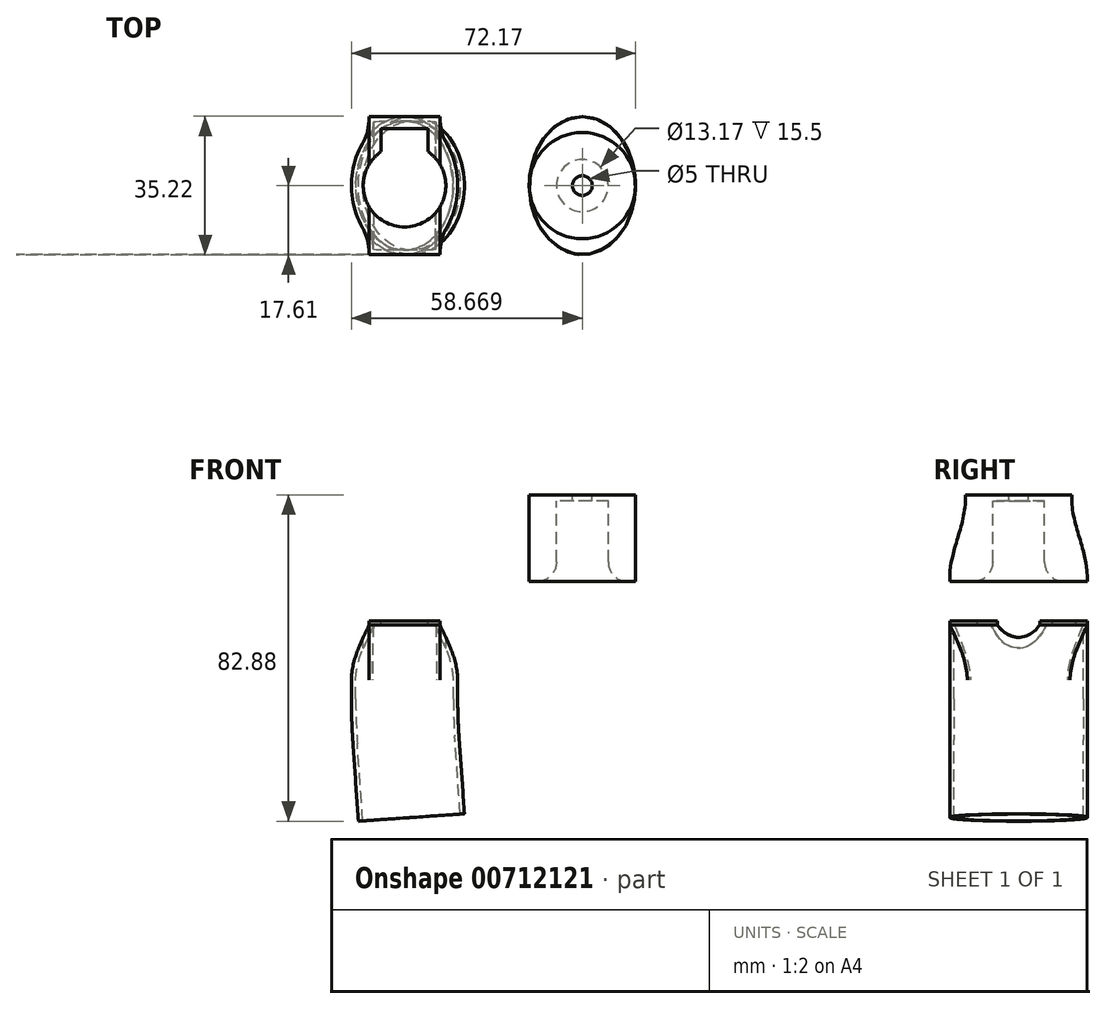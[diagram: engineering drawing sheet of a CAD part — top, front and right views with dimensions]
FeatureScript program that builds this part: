
annotation { "Feature Type Name" : "Feature", "Feature Type Description" : "" }
export const myFeature = defineFeature(function(context is Context, id is Id, definition is map)
    precondition{}
    {
        {
            var Q0;
            Q0=qCreatedBy(makeId("Top.planeOp"),FACE);
            var sketch = newSketch(context, id + "F0", { "sketchPlane" : qUnion([Q0])});
            skLineSegment(sketch, "E0.bottom", {"start": v(-9, 17.5) * mm, "end": v(9, 17.5) * mm});
            skLineSegment(sketch, "E0.top", {"start": v(-9, -17.5) * mm, "end": v(9, -17.5) * mm});
            skLineSegment(sketch, "E0.left", {"start": v(-9, 17.5) * mm, "end": v(-9, -17.5) * mm});
            skLineSegment(sketch, "E0.right", {"start": v(9, 17.5) * mm, "end": v(9, -17.5) * mm});
            skSolve(sketch);
        }
        {
            var Q0;
            Q0=makeQuery(id+"F0.imprint","IMPRINT",FACE,{"disambiguationData":[TD([[makeQuery(id+"F0.imprint","IMPRINT",EDGE,{"derivedFrom":sQuery(id+"F0.wireOp",EDGE,"E0.bottom")}),-1.0]])]});
            extrude(context, id + "F1", {"entities" : qUnion([Q0]), "depth" : 15 * mm, "offsetDistance" : 25 * mm, "hasSecondDirection" : true, "secondDirectionOppositeDirection" : false, "secondDirectionDepth" : 14 * mm});
        }
        {
            var Q0;
            Q0=qCreatedBy(makeId("Top.planeOp"),FACE);
            var sketch = newSketch(context, id + "F2", { "sketchPlane" : qUnion([Q0])});
            skEllipticalArc(sketch, "E1", {});
            skEllipticalArc(sketch, "E2", {});
            skEllipticalArc(sketch, "E3", {});
            skEllipticalArc(sketch, "E4", {});
            const initialGuessF2  = {"E1": [0, 0, 0, 1, 0.0175, 0.0135, 3.8715789062969574, 5.5567192780219345], "E2": [0, 0, 0, 1, 0.0175, 0.0135, 2.4065715334507507, 3.8715789062969574], "E3": [0, 0, 0, 1, 0.0175, 0.0135, 5.5567192780219345, 0.7288720705966393], "E4": [0, 0, 0, 1, 0.0175, 0.0135, 0.7288720705966393, 2.4065715334507507]};
            skSetInitialGuess(sketch, initialGuessF2);
            skSolve(sketch);
        }
        {
            var Q1;
            Q1=makeQuery(id+"F1.opExtrude","CAP_FACE",FACE,{"disambiguationData":[OSD([sQuery(id+"F0.wireOp",EDGE,"E0.bottom"),sQuery(id+"F0.wireOp",EDGE,"E0.top"),sQuery(id+"F0.wireOp",EDGE,"E0.left"),sQuery(id+"F0.wireOp",EDGE,"E0.right")])],"isStart":true});
            var Q2;
            Q2=makeQuery(id+"F2.imprint","IMPRINT",FACE,{"disambiguationData":[TD([[makeQuery(id+"F2.imprint","IMPRINT",EDGE,{"derivedFrom":sQuery(id+"F2.wireOp",EDGE,"E1")}),1.0]])]});
            loft(context, id + "F3", {"operationType" : NewBodyOperationType.ADD, "endCondition" : LoftEndDerivativeType.NORMAL_TO_PROFILE, "endMagnitude" : 1, "sheetProfilesArray" : [{ "sheetProfileEntities" : qUnion([Q1]) }, { "sheetProfileEntities" : qUnion([Q2]) }]});
        }
        {
            var Q0;
            Q0=qCreatedBy(makeId("Top.planeOp"),FACE);
            cPlane(context, id + "F4", {"entities" : qUnion([Q0]), "cplaneType" : CPlaneType.OFFSET, "offset" : 25 * mm, "width" : 150 * mm, "height" : 150 * mm});
        }
        {
            var Q0;
            Q0=makeQuery(id+"F3.opLoft","CAP_FACE",FACE,{"disambiguationData":[OSD([makeQuery(id+"F2.imprint","IMPRINT",FACE,{"disambiguationData":[TD([[makeQuery(id+"F2.imprint","IMPRINT",EDGE,{"derivedFrom":sQuery(id+"F2.wireOp",EDGE,"E1")}),1.0]])]})])],"isStart":true});
            shell(context, id + "F5", {"entities" : qUnion([Q0]), "thickness" : 1.1 * mm});
        }
        {
            var Q0;
            Q0=makeQuery(id+"F1.opExtrude","CAP_FACE",FACE,{"disambiguationData":[OSD([sQuery(id+"F0.wireOp",EDGE,"E0.bottom"),sQuery(id+"F0.wireOp",EDGE,"E0.top"),sQuery(id+"F0.wireOp",EDGE,"E0.left"),sQuery(id+"F0.wireOp",EDGE,"E0.right")])],"isStart":false});
            var sketch = newSketch(context, id + "F6", { "sketchPlane" : qUnion([Q0])});
            skCircle(sketch, "E5", {"center": v(0, 0) * mm, "radius": 10.5 * mm});
            skLineSegment(sketch, "E6.bottom", {"start": v(-6, 14.54) * mm, "end": v(6, 14.54) * mm});
            skLineSegment(sketch, "E6.top", {"start": v(-6, 7.06) * mm, "end": v(6, 7.06) * mm});
            skLineSegment(sketch, "E6.left", {"start": v(-6, 14.54) * mm, "end": v(-6, 7.06) * mm});
            skLineSegment(sketch, "E6.right", {"start": v(6, 14.54) * mm, "end": v(6, 7.06) * mm});
            skSolve(sketch);
        }
        {
            var Q0;
            {var subQ0=sQuery(id+"F6.wireOp",EDGE,"E5");var subQ1=makeQuery(id+"F1.opExtrude","CAP_EDGE",EDGE,{"disambiguationData":[OSD([sQuery(id+"F0.wireOp",EDGE,"E0.left")])],"isStart":false});var subQ2=makeQuery(id+"F6.imprint","INTERSECT",VERTEX,{"disambiguationData":[OD(0.0)],"derivedFrom":[subQ1,subQ0]});Q0=makeQuery(id+"F6.imprint","IMPRINT",FACE,{"disambiguationData":[TD([[makeQuery(id+"F6.imprint","IMPRINT",EDGE,{"disambiguationData":[TD([[subQ2,1.0]])],"derivedFrom":subQ0}),1.0]])]});}
            var Q1;
            {var subQ0=sQuery(id+"F6.wireOp",EDGE,"E5");var subQ1=makeQuery(id+"F1.opExtrude","CAP_EDGE",EDGE,{"disambiguationData":[OSD([sQuery(id+"F0.wireOp",EDGE,"E0.left")])],"isStart":false});var subQ2=makeQuery(id+"F6.imprint","INTERSECT",VERTEX,{"disambiguationData":[OD(0.0)],"derivedFrom":[subQ1,subQ0]});Q1=makeQuery(id+"F6.imprint","IMPRINT",FACE,{"disambiguationData":[TD([[makeQuery(id+"F6.imprint","IMPRINT",EDGE,{"disambiguationData":[TD([[subQ2,-1.0]])],"derivedFrom":subQ0}),1.0]])]});}
            var Q2;
            {var subQ0=sQuery(id+"F6.wireOp",EDGE,"E5");var subQ1=makeQuery(id+"F1.opExtrude","CAP_EDGE",EDGE,{"disambiguationData":[OSD([sQuery(id+"F0.wireOp",EDGE,"E0.right")])],"isStart":false});var subQ2=makeQuery(id+"F6.imprint","INTERSECT",VERTEX,{"disambiguationData":[OD(0.0)],"derivedFrom":[subQ1,subQ0]});Q2=makeQuery(id+"F6.imprint","IMPRINT",FACE,{"disambiguationData":[TD([[makeQuery(id+"F6.imprint","IMPRINT",EDGE,{"disambiguationData":[TD([[subQ2,1.0]])],"derivedFrom":subQ0}),1.0]])]});}
            var Q3;
            {var subQ5=sQuery(id+"F6.wireOp",EDGE,"E6.bottom");Q3=makeQuery(id+"F6.imprint","IMPRINT",FACE,{"disambiguationData":[TD([[makeQuery(id+"F6.imprint","IMPRINT",EDGE,{"derivedFrom":subQ5}),-1.0]])]});}
            var Q4;
            {var subQ5=sQuery(id+"F6.wireOp",EDGE,"E6.top");Q4=makeQuery(id+"F6.imprint","IMPRINT",FACE,{"disambiguationData":[TD([[makeQuery(id+"F6.imprint","IMPRINT",EDGE,{"derivedFrom":subQ5}),1.0]])]});}
            extrude(context, id + "F7", {"entities" : qUnion([Q0, Q1, Q2, Q3, Q4]), "operationType" : NewBodyOperationType.REMOVE, "oppositeDirection" : true, "depth" : 10 * mm, "offsetDistance" : 25 * mm});
        }
        {
            var Q0;
            Q0=makeQuery(id+"F3.opLoft","CAP_FACE",FACE,{"disambiguationData":[OSD([makeQuery(id+"F2.imprint","IMPRINT",FACE,{"disambiguationData":[TD([[makeQuery(id+"F2.imprint","IMPRINT",EDGE,{"derivedFrom":sQuery(id+"F2.wireOp",EDGE,"E1")}),1.0]])]})])],"isStart":true});
            var sketch = newSketch(context, id + "F8", { "sketchPlane" : qUnion([Q0])});
            skEllipse(sketch, "E7", {"center": v(0, 0) * mm, "majorRadius": 13.51 * mm, "minorRadius": 17.52 * mm, "majorAxis": v(1, 0)});
            skSolve(sketch);
        }
        {
            var Q0;
            Q0=qCreatedBy(makeId("Front.planeOp"),FACE);
            var sketch = newSketch(context, id + "F9", { "sketchPlane" : qUnion([Q0])});
            skLineSegment(sketch, "E8", {"start": v(0, 0) * mm, "end": v(0, -4.76) * mm});
            skLineSegment(sketch, "E9", {"start": v(0.37, -15.23) * mm, "end": v(1.74, -34.94) * mm});
            skPoint(sketch, "E10.visualSharp", {"position": v(0, -10) * mm});
            skArc(sketch, "E10.filletArc", {"start": v(0, -4.76) * mm, "mid": v(0.1, -10) * mm, "end": v(0.37, -15.23) * mm});
            skLineSegment(sketch, "E11", {"start": v(1.74, -34.94) * mm, "end": v(4.83, -79.09) * mm});
            skSolve(sketch);
        }
        {
            var Q0;
            {var subQ1=sQuery(id+"F2.wireOp",EDGE,"E3");var subQ2=sQuery(id+"F2.wireOp",EDGE,"E2");var subQ3=sQuery(id+"F2.wireOp",EDGE,"E1");Q0=makeQuery(id+"F8.imprint","IMPRINT",FACE,{"disambiguationData":[TD([[makeQuery(id+"F8.imprint","IMPRINT",EDGE,{"derivedFrom":makeQuery(id+"F3.opLoft","MID_CAP_EDGE",EDGE,{"disambiguationData":[OSD([subQ3,subQ2,subQ1])],"capPos":1.0})}),1.0]])]});}
            var Q1;
            Q1=sQuery(id+"F9.wireOp",EDGE,"E9");
            var Q2;
            Q2=sQuery(id+"F9.wireOp",EDGE,"E10.filletArc");
            var Q3;
            Q3=sQuery(id+"F9.wireOp",EDGE,"E8");
            sweep(context, id + "F10", {"operationType" : NewBodyOperationType.ADD, "profiles" : qUnion([Q0]), "path" : qUnion([Q1, Q2, Q3])});
        }
        {
            var Q0;
            Q0=qCreatedBy(id+"F4.planeOp",FACE);
            var sketch = newSketch(context, id + "F11", { "sketchPlane" : qUnion([Q0])});
            skCircle(sketch, "E12", {"center": v(45.17, 0) * mm, "radius": 13.5 * mm});
            skEllipse(sketch, "E13", {"center": v(45.17, 0) * mm, "majorRadius": 17.5 * mm, "minorRadius": 13.5 * mm, "majorAxis": v(0, 1)});
            skSolve(sketch);
        }
        {
            var Q0;
            Q0=makeQuery(id+"F11.imprint","IMPRINT",FACE,{"disambiguationData":[TD([[makeQuery(id+"F11.imprint","IMPRINT",EDGE,{"derivedFrom":sQuery(id+"F11.wireOp",EDGE,"E12")}),1.0]])]});
            extrude(context, id + "F12", {"entities" : qUnion([Q0]), "depth" : 22 * mm, "offsetDistance" : 25 * mm, "hasSecondDirection" : true, "secondDirectionOppositeDirection" : false, "secondDirectionDepth" : 21 * mm});
        }
        {
            var Q0;
            {var subQ0=sQuery(id+"F11.wireOp",EDGE,"E13");var subQ1=sQuery(id+"F11.wireOp",EDGE,"E12");var subQ2=makeQuery(id+"F11.imprint","INTERSECT",VERTEX,{"disambiguationData":[OD(0.0)],"derivedFrom":[subQ1,subQ0]});Q0=makeQuery(id+"F11.imprint","IMPRINT",FACE,{"disambiguationData":[TD([[makeQuery(id+"F11.imprint","IMPRINT",EDGE,{"disambiguationData":[TD([[subQ2,1.0]])],"derivedFrom":subQ1}),-1.0]])]});}
            var Q1;
            {var subQ0=sQuery(id+"F11.wireOp",EDGE,"E13");var subQ1=sQuery(id+"F11.wireOp",EDGE,"E12");var subQ2=makeQuery(id+"F11.imprint","INTERSECT",VERTEX,{"disambiguationData":[OD(0.0)],"derivedFrom":[subQ1,subQ0]});Q1=makeQuery(id+"F11.imprint","IMPRINT",FACE,{"disambiguationData":[TD([[makeQuery(id+"F11.imprint","IMPRINT",EDGE,{"disambiguationData":[TD([[subQ2,-1.0]])],"derivedFrom":subQ1}),-1.0]])]});}
            var Q2;
            {var subQ0=sQuery(id+"F11.wireOp",EDGE,"E13");var subQ1=sQuery(id+"F11.wireOp",EDGE,"E12");var subQ2=makeQuery(id+"F11.imprint","INTERSECT",VERTEX,{"disambiguationData":[OD(0.0)],"derivedFrom":[subQ1,subQ0]});Q2=makeQuery(id+"F11.imprint","IMPRINT",FACE,{"disambiguationData":[TD([[makeQuery(id+"F11.imprint","IMPRINT",EDGE,{"disambiguationData":[TD([[subQ2,1.0]])],"derivedFrom":subQ1}),1.0]])]});}
            extrude(context, id + "F13", {"entities" : qUnion([Q0, Q1, Q2]), "depth" : 1 * mm, "offsetDistance" : 25 * mm});
        }
        {
            var Q1;
            Q1=makeQuery(id+"F12.opExtrude","CAP_FACE",FACE,{"disambiguationData":[OSD([sQuery(id+"F11.wireOp",EDGE,"E12")])],"isStart":true});
            var Q2;
            Q2=makeQuery(id+"F13.opExtrude","CAP_FACE",FACE,{"disambiguationData":[OSD([sQuery(id+"F11.wireOp",EDGE,"E13")])],"isStart":false});
            loft(context, id + "F14", {"operationType" : NewBodyOperationType.ADD, "startCondition" : LoftEndDerivativeType.MATCH_TANGENT, "startMagnitude" : 1, "endCondition" : LoftEndDerivativeType.MATCH_TANGENT, "endMagnitude" : 1, "sheetProfilesArray" : [{ "sheetProfileEntities" : qUnion([Q1]) }, { "sheetProfileEntities" : qUnion([Q2]) }]});
        }
        {
            var Q0;
            Q0=makeQuery(id+"F12.opExtrude","CAP_FACE",FACE,{"disambiguationData":[OSD([sQuery(id+"F11.wireOp",EDGE,"E12")])],"isStart":false});
            var sketch = newSketch(context, id + "F15", { "sketchPlane" : qUnion([Q0])});
            skCircle(sketch, "E14", {"center": v(45.17, 0) * mm, "radius": 6.58 * mm});
            skCircle(sketch, "E15", {"center": v(45.17, 0) * mm, "radius": 2.5 * mm});
            skSolve(sketch);
        }
        {
            var Q0;
            Q0=makeQuery(id+"F15.imprint","IMPRINT",FACE,{"disambiguationData":[TD([[makeQuery(id+"F15.imprint","IMPRINT",EDGE,{"derivedFrom":sQuery(id+"F15.wireOp",EDGE,"E14")}),1.0]])]});
            extrude(context, id + "F16", {"entities" : qUnion([Q0]), "operationType" : NewBodyOperationType.REMOVE, "oppositeDirection" : true, "depth" : 25 * mm, "offsetDistance" : 25 * mm, "hasSecondDirection" : true, "secondDirectionOppositeDirection" : true, "secondDirectionDepth" : 1.5 * mm});
        }
        {
            var Q0;
            Q0=makeQuery(id+"F15.imprint","IMPRINT",FACE,{"disambiguationData":[TD([[makeQuery(id+"F15.imprint","IMPRINT",EDGE,{"derivedFrom":sQuery(id+"F15.wireOp",EDGE,"E15")}),1.0]])]});
            extrude(context, id + "F17", {"entities" : qUnion([Q0]), "operationType" : NewBodyOperationType.REMOVE, "oppositeDirection" : true, "depth" : 25 * mm, "offsetDistance" : 25 * mm});
        }
        {
            var Q0;
            Q0=makeQuery(id+"F16.boolean.opBoolean","INTERSECT",EDGE,{"derivedFrom":[makeQuery(id+"F13.opExtrude","CAP_FACE",FACE,{"disambiguationData":[OSD([sQuery(id+"F11.wireOp",EDGE,"E13")])],"isStart":true}),makeQuery(id+"F16.opExtrude","SWEPT_FACE",FACE,{"disambiguationData":[OSD([sQuery(id+"F15.wireOp",EDGE,"E14")])]})]});
            fillet(context, id + "F18", {"entities" : qUnion([Q0]), "radius" : 5 * mm, "tangentPropagation" : true, "allowEdgeOverflow" : false});
        }
    });
